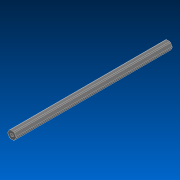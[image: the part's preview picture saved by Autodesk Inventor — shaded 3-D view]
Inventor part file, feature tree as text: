
AUTODESK INVENTOR PART (.ipt)
format: ipt  version: 2022.2 (Build 262287000, 287)  size: 121,344 bytes
history: native  units: in
note: dims shown in document units (in); Inventor stores cm internally (conversion verified against a paired STEP export)
features: extrude x1, sketch x1, other x1
ambient origin geometry x8: Origin, YZ Plane, XZ Plane, XY Plane, X Axis, Y Axis, Z Axis, Center Point
bodies: Solid1 (feature_tree)
feature tree (3):
  extrude  "Extrusion1"  TaperAngle=0.0deg  [1 undecoded]
  sketch  "Sketch1"  dims[d0=25.7in d1=0.0in]
  other  "Cut-Extrude2"
note: 1 required parameter value undecoded (feature->parameter linkage not recoverable at this tier; creation-order binding heuristic only, values carry confidence <= 0.55)
